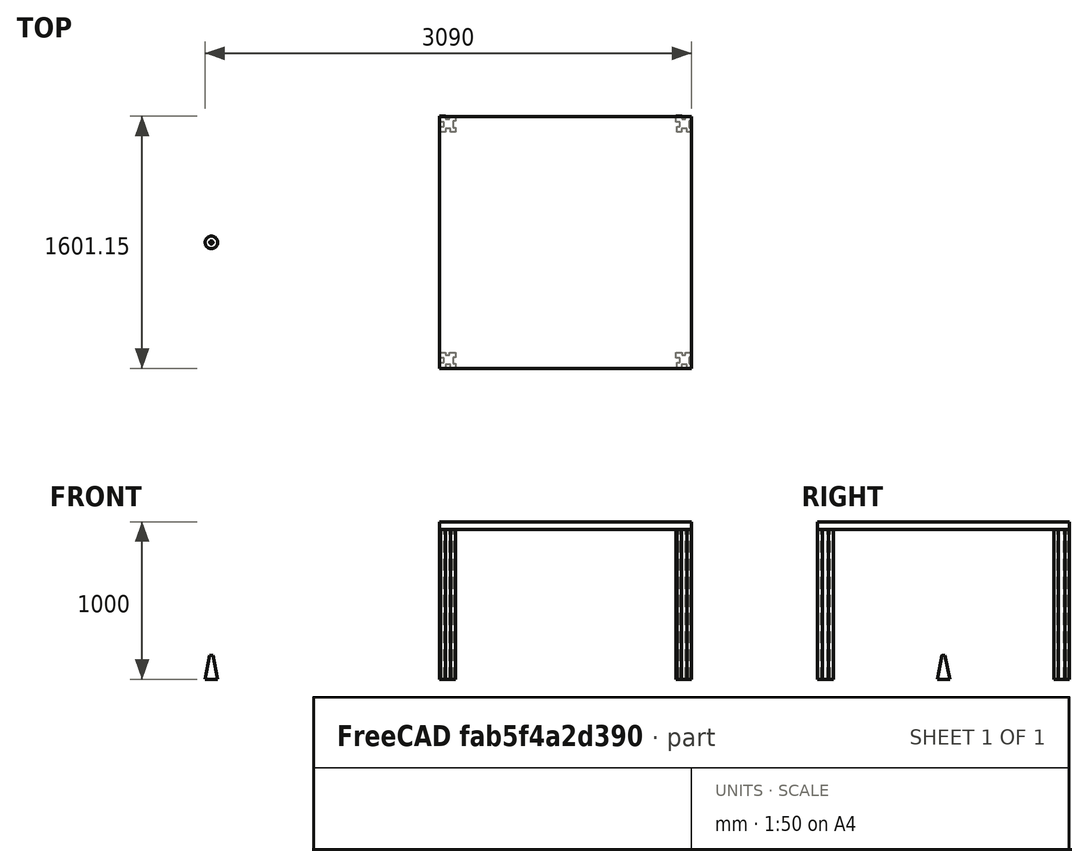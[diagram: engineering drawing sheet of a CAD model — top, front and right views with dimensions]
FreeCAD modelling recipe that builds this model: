
FCSTD DOCUMENT  (FreeCAD 0.19R17171 (Git))
Label: RobotExample
License: CreativeCommons Attribution
LicenseURL: http://creativecommons.org/licenses/by/4.0/
objects: PartDesign::Pad×5, Part::Plane×1, Part::Box×1, Sketcher::SketchObjectSF×1, Robot::TrajectoryObject×1, Robot::RobotObject×1, Part::Cone×1, App::DocumentObjectGroup×1
note: 14 computed .brp shape members not serialized (recipe doc carries the construction recipe); baked Part::Feature solids carry a one-line shape summary decoded from their .brp

FEATURE [Part::Plane] Plane
  AttacherType = Attacher::AttachEngine3D
  Length = 10000
  Placement = pos=(-5000,-5000,0) rot=(0,0,1;0rad)
  Width = 10000
FEATURE [PartDesign::Pad] Pad  label="Bein1"
  Length = 100
  Length2 = 100
  Placement = pos=(1500,-750,0) rot=(0,0,1;0rad)
  Type = 0
FEATURE [PartDesign::Pad] Pad1  label="Bein2"
  Length = 100
  Length2 = 100
  Placement = pos=(1500,750,0) rot=(0,0,1;0rad)
  Type = 0
FEATURE [PartDesign::Pad] Pad2  label="Bein3"
  Length = 100
  Length2 = 100
  Placement = pos=(3000,-750,0) rot=(0,0,1;0rad)
  Type = 0
FEATURE [PartDesign::Pad] Pad3  label="Bein4"
  Length = 100
  Length2 = 100
  Placement = pos=(3000,750,0) rot=(0,0,1;0rad)
  Type = 0
FEATURE [Part::Box] Box  label="TischPlatte"
  AttacherType = Attacher::AttachEngine3D
  Height = 50
  Length = 1600
  Placement = pos=(1450,-800,950) rot=(0,0,1;0rad)
  Width = 1600
FEATURE [Sketcher::SketchObjectSF] Sketch
  MapMode = 5
FEATURE [PartDesign::Pad] Pad4  label="PartToWork"
  Length = 100
  Length2 = 100
  Placement = pos=(2217.27,-81.4724,1513.01) rot=(0,0,1;0rad)
  Type = 0
FEATURE [Robot::TrajectoryObject] Trajectory
FEATURE [Robot::RobotObject] Robot
  Axis1 = -5.7679e-12
  Axis2 = -90.0001
  Axis3 = 90
  Axis4 = 4.72328e-11
  Axis5 = 45.0001
  Axis6 = 2.9999
  Home = [0]
  Tcp = pos=(1737.13,-1.511e-13,2187.87) rot=(-0.026175,0.999599,-0.010842;2.35648rad)
FEATURE [Part::Cone] Cone  label="ToolShape"
  Angle = 360
  AttacherType = Attacher::AttachEngine3D
  Height = 150
  Radius1 = 40
  Radius2 = 10
FEATURE [App::DocumentObjectGroup] Gruppe  label="SetUp"
  Group = -> [Plane,Pad,Pad1,Pad2,Pad3,Box,Sketch,Cone]
